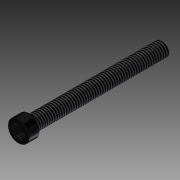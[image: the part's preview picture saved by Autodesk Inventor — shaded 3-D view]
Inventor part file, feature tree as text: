
AUTODESK INVENTOR PART (.ipt)
format: ipt  version: 2013 (Build 170138000, 138)  size: 107,520 bytes
history: native  units: in
note: dims shown in document units (in); Inventor stores cm internally (conversion verified against a paired STEP export)
features: extrude x3, sketch x1, thread x1, chamfer x1
ambient origin geometry x8: Origin, YZ Plane, XZ Plane, XY Plane, X Axis, Y Axis, Z Axis, Center Point
bodies: Solid1 (feature_tree)
feature tree (6):
  sketch  "Sketch1"  dims[d0=0.275in d1=0.185in d2=0.15in d3=0.15in d4=0.0in d5=1.715in d6=0.0in d7=0.05in d8=0.0in d9=1.0in d10=0.0in d11=0.01in d12=0.125in d13=45.0deg]
  extrude  "Extrusion1"  Depth=0.185in
  extrude  "Extrusion2"  Depth=0.15in
  extrude  "Extrusion3"  Depth=0.15in TaperAngle=0.0deg
  thread  "Thread1"  [1 undecoded]
  chamfer  "Chamfer1"  Distance=0.05in
note: 1 required parameter value undecoded (feature->parameter linkage not recoverable at this tier; creation-order binding heuristic only, values carry confidence <= 0.55)
